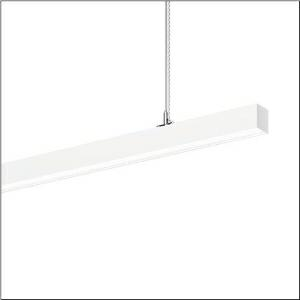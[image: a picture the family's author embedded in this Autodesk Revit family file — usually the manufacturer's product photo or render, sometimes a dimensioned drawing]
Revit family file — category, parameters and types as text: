
# Revit family: silica_r__21_51mx33tat7w_2751
name_source: partatom
category: Lighting Fixtures
units: mm (PartAtom-declared; Revit-internal decimal feet)

## family parameters
Cut with Voids When Loaded = No
Host = Face
Light Source = No
Part Type = Normal
Room Calculation Point = No
Round Connector Dimension = Use Diameter
Shared = No

## types (1)
- --- (1 x LED, 5740 lm, 53.8 W, 6500K)
    Apparent Load = 54 VA
    CIE Flux Codes = 78 96 99 56 100
    Color Rendering = 80
    Color Temperature = 6500K
    Default Elevation = 1800 mm
    Description = Silica® 21, office luminaire, primary optical cover: prismatic diffuser, of PMMA, CAT 2 (L<= 3000cd/m²), light emission: direct/indirect distribution, primary light characteristic: symmetric, installation type: suspended mounting, LED, rated luminous flux: 5.740lm, luminous efficacy: 102lm/W, light colour: 8tw, colour temperature: 2700..6500K, control gear: DALI DT8, with terminal, 3+2-pole, max. 2.5mm², mains connection: 220..240V, AC, 50/60Hz, rated input power: 56.5W, luminaire housing, of aluminium, traffic white (RAL 9016), length: 1.204mm, width: 53mm, height: 53mm, protection rating (complete): IP20, insulation class (complete): insulation class I (protective earthing), certification: CE, permissible operating ambient temperature: 0..+35°C, standard: EN 50419, packaging unit: 1 piece
    Height = 53 mm
    Lamp = 1 x LED
    Lamp Light Flux = 5740 lm
    Lamp Power = 53.8 W
    Lamp count = 1
    Length = 1204 mm
    Luminous efficacy = 107 lm/W
    Manufacturer = Siteco
    ModVariant = No
    Model = 51MX33TAT7W
    Mounting Place = Ceiling
    Mounting Type = Pendant
    Number of Poles = 1
    OnlyDefault = Yes
    Power Factor = 1
    Product Name = Silica® 21
    Product group = office luminaire | ceiling pendant
    ProductGroupID = 903
    Protection Class = Protection class I
    Protection Degree = IP 20
    RLX_Detail_Level = 1
    RLX_Emergency_Light_Flux = 0 lm
    RLX_Emergency_Type = 0
    RLX_Emergency_Type_DB = No
    RlxData = <blob elided: 18177 chars, md5=e0fc1708>
    Socket = socket
    Standby Power = 0 W
    System Light Flux = 5740 lm
    System Power = 54 W
    Type Comments = individual setting
    Type Image = l_1349007.jpg
    URL = http://relux.com
    VarID = @adj_161261
    Voltage = 0 V
    Weight = 0.00 kg
    Width = 53 mm

## geometry (parser evidence)
native form markers: Blend x4, Sweep x14
no freeform markers — native parametric forms only
